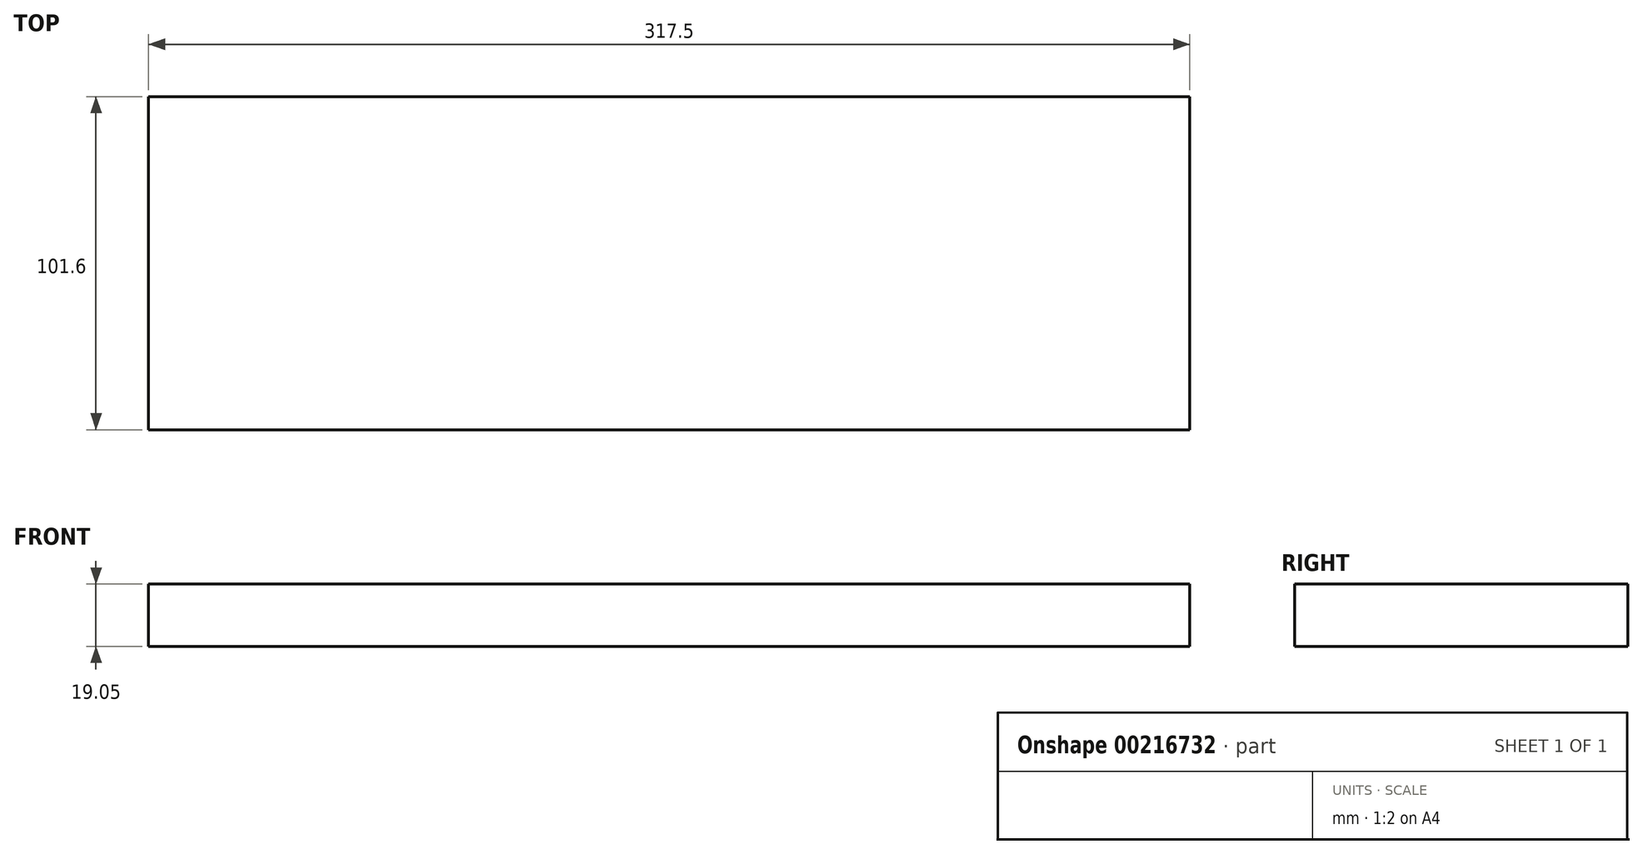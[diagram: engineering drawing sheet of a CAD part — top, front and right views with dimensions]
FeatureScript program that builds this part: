
annotation { "Feature Type Name" : "Feature", "Feature Type Description" : "" }
export const myFeature = defineFeature(function(context is Context, id is Id, definition is map)
    precondition{}
    {
        {
            var Q0;
            Q0=qCreatedBy(makeId("Top.planeOp"),FACE);
            var sketch = newSketch(context, id + "F0", { "sketchPlane" : qUnion([Q0])});
            skLineSegment(sketch, "E0.bottom", {"start": v(0, 0) * mm, "end": v(317.5, 0) * mm});
            skLineSegment(sketch, "E0.top", {"start": v(0, 101.6) * mm, "end": v(317.5, 101.6) * mm});
            skLineSegment(sketch, "E0.left", {"start": v(0, 0) * mm, "end": v(0, 101.6) * mm});
            skLineSegment(sketch, "E0.right", {"start": v(317.5, 0) * mm, "end": v(317.5, 101.6) * mm});
            skSolve(sketch);
        }
        {
            var Q0;
            Q0 = qSketchRegion(id + "F0", true);
            extrude(context, id + "F1", {"entities" : qUnion([Q0]), "depth" : 19.05 * mm});
        }
    });
